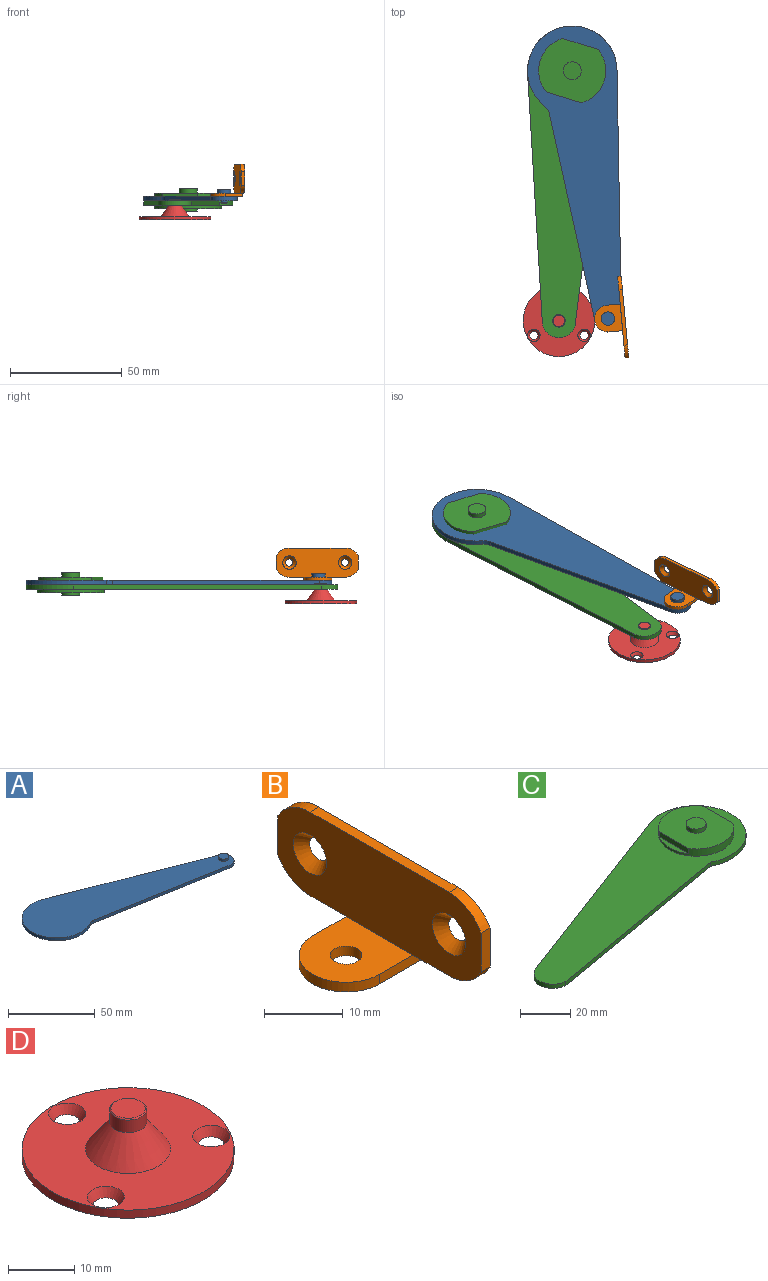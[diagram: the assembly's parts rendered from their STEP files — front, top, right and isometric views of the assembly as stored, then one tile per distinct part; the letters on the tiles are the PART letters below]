
ASSEMBLY  parts=4 mates=3
PART A: 14 faces, bbox 134.5x53.5x6 mm
  f0: plane 103.39x40.53mm, normal (0.37,0.93,0), area 222.1mm2, adj f1,f4,f5,f6
  f1: cylinder r=20mm len=40mm, axis (0,0,-1), area 161.6mm2, adj f0,f2,f5,f6
  f2: cylinder r=5mm len=3.37mm, axis (0,0,-1), area 7mm2, adj f1,f3,f5,f6
  f3: plane 93.08x16.41mm, normal (-0.17,-0.98,0), area 189mm2, adj f2,f4,f5,f6
  f4: cylinder r=6mm len=11.59mm, axis (0,0,-1), area 37.4mm2, adj f0,f3,f5,f6
  f5: plane 134.5x53.5mm, normal (0,0,1), area 3334.7mm2, adj f0,f1,f2,f3,f4,f13
  f6: plane 134.5x53.5mm, normal (0,0,-1), area 3334.7mm2, adj f0,f1,f2,f3,f4,f9
  f7: plane 2.4x2.4mm, normal (0,0,-1), area 4.5mm2, adj f8
  f8: cone r=1.5mm half-angle=45deg, axis (0,0,1), area 3.6mm2, adj f7,f9
  f9: cylinder r=1.5mm len=3mm, axis (0,0,-1), area 6.6mm2, adj f6,f8
  f10: plane 6x6mm, normal (0,0,1), area 28.3mm2, adj f11
  f11: cylinder r=3mm len=6mm, axis (0,0,-1), area 28.3mm2, adj f10,f12
  f12: plane 6x6mm, normal (0,0,-1), area 21.2mm2, adj f11,f13
  f13: cylinder r=1.5mm len=3mm, axis (0,0,-1), area 14.1mm2, adj f5,f12
PART B: 19 faces, bbox 13.6x36.5x14.5 mm
  f0: plane 25x1.6mm, normal (0,0,1), area 40mm2, adj f1,f2,f15,f16
  f1: plane 36.5x14.5mm, normal (1,0,0), area 452.5mm2, adj f0,f3,f5,f7,f8,f9,f11,f12
  f2: plane 36.5x13mm, normal (-1,0,0), area 395mm2, adj f0,f7,f8,f10,f11,f12,f13,f14
  f3: plane 7.6x1.5mm, normal (0,1,0), area 11.4mm2, adj f1,f4,f9,f10,f13
  f4: cylinder r=6mm len=12mm, axis (0,0,-1), area 28.3mm2, adj f3,f5,f9,f10
  f5: plane 7.6x1.5mm, normal (0,-1,0), area 11.4mm2, adj f1,f4,f9,f10,f12
  f6: cylinder r=2mm len=4mm, axis (0,0,-1), area 18.8mm2, adj f9,f10
  f7: plane 6.06x1.6mm, normal (0,-1,0), area 9.7mm2, adj f1,f2,f11,f15
  f8: plane 6.06x1.6mm, normal (0,1,0), area 9.7mm2, adj f1,f2,f14,f16
  f9: plane 13.6x12mm, normal (0,0,-1), area 135.2mm2, adj f1,f3,f4,f5,f6
  f10: plane 12x12mm, normal (0,0,1), area 116mm2, adj f2,f3,f4,f5,f6
  f11: cylinder r=6.5mm len=5.75mm, axis (-1,0,0), area 11.3mm2, adj f1,f2,f7,f12
  f12: plane 6.5x1.6mm, normal (0,0,-1), area 10.4mm2, adj f1,f2,f5,f11
  f13: plane 6.5x1.6mm, normal (0,0,-1), area 10.4mm2, adj f1,f2,f3,f14
  f14: cylinder r=6.5mm len=5.75mm, axis (-1,0,0), area 11.3mm2, adj f1,f2,f8,f13
  f15: cylinder r=6.5mm len=5.75mm, axis (-1,0,0), area 11.3mm2, adj f0,f1,f2,f7
  f16: cylinder r=6.5mm len=5.75mm, axis (-1,0,0), area 11.3mm2, adj f0,f1,f2,f8
  f17: cone r=3mm half-angle=40.2deg, axis (-1,0,0), area 30.6mm2, adj f1,f2
  f18: cone r=3mm half-angle=40.2deg, axis (-1,0,0), area 30.6mm2, adj f1,f2
PART C: 18 faces, bbox 136x55x10 mm
  f0: plane 104.1x39.2mm, normal (-0.35,0.94,0), area 222.5mm2, adj f1,f3,f4,f5
  f1: cylinder r=7.5mm len=14.52mm, axis (0,0,-1), area 41.7mm2, adj f0,f2,f4,f5
  f2: plane 98.92x17.44mm, normal (0.17,-0.98,0), area 200.9mm2, adj f1,f3,f4,f5
  f3: cylinder r=20mm len=40mm, axis (0,0,-1), area 160mm2, adj f0,f2,f4,f5
  f4: plane 136x55mm, normal (0,0,1), area 2892.8mm2, adj f0,f1,f2,f3,f13
  f5: plane 136x55mm, normal (0,0,-1), area 2892.8mm2, adj f0,f1,f2,f3,f9
  f6: plane 8x8mm, normal (0,0,-1), area 50.3mm2, adj f7
  f7: cylinder r=4mm len=8mm, axis (0,0,-1), area 25.1mm2, adj f6,f8
  f8: plane 30x30mm, normal (0,0,-1), area 656.6mm2, adj f7,f9
  f9: cylinder r=15mm len=30mm, axis (0,0,-1), area 141.4mm2, adj f5,f8
  f10: plane 8x8mm, normal (0,0,1), area 50.3mm2, adj f11
  f11: cylinder r=4mm len=8mm, axis (0,0,-1), area 50.3mm2, adj f10,f12
  f12: plane 30x25mm, normal (0,0,1), area 600.3mm2, adj f11,f13,f15,f16
  f13: cylinder r=15mm len=30mm, axis (0,0,-1), area 242mm2, adj f4,f12,f14,f15,f16,f17
  f14: plane 16.58x2.5mm, normal (0,0,1), area 28.1mm2, adj f13,f15
  f15: plane 16.58x2.5mm, normal (1,0,0), area 41.5mm2, adj f12,f13,f14
  f16: plane 16.58x2.5mm, normal (-1,0,0), area 41.5mm2, adj f12,f13,f17
  f17: plane 16.58x2.5mm, normal (0,0,1), area 28.1mm2, adj f13,f16
PART D: 10 faces, bbox 32x32x9 mm
  f0: cylinder r=16mm len=32mm, axis (0,0,-1), area 150.8mm2, adj f1,f2
  f1: plane 32x32mm, normal (0,0,1), area 601.1mm2, adj f0,f6,f7,f8,f9
  f2: plane 32x32mm, normal (0,0,-1), area 770.2mm2, adj f0,f7,f8,f9
  f3: plane 5.2x5.2mm, normal (0,0,1), area 21.2mm2, adj f4
  f4: cone r=2.6mm half-angle=45deg, axis (0,0,-1), area 4.8mm2, adj f3,f5
  f5: cylinder r=2.8mm len=5.6mm, axis (0,0,-1), area 40.5mm2, adj f4,f6
  f6: cone r=2.8mm half-angle=35.9deg, axis (0,0,-1), area 178.6mm2, adj f1,f5
  f7: cone r=2.8mm half-angle=31deg, axis (0,0,1), area 25.8mm2, adj f1,f2
  f8: cone r=2.8mm half-angle=31deg, axis (0,0,1), area 25.8mm2, adj f1,f2
  f9: cone r=2.8mm half-angle=31deg, axis (0,0,1), area 25.8mm2, adj f1,f2
PLACE A rot(axis=(0,0,-1),67.6deg) t=(-19.5,101.28,2)mm
PLACE B rot(axis=(0,0,1),5.3deg) t=(21.92,0.99,4)mm
PLACE C rot(axis=(0,0,1),72.7deg) t=(0,0,1)mm
PLACE D t=(0,0,-6.5)mm fixed
MATE revolute A.f1 <-> C.f3  axis (0,0,-1) through (5.92,111.77,2)mm
MATE revolute C.f1 <-> D.f0  axis (0,0,-1) through (0,0,0)mm
MATE revolute B.f4 <-> A.f8  axis (0,0,1) through (21.92,0.99,5.5)mm
